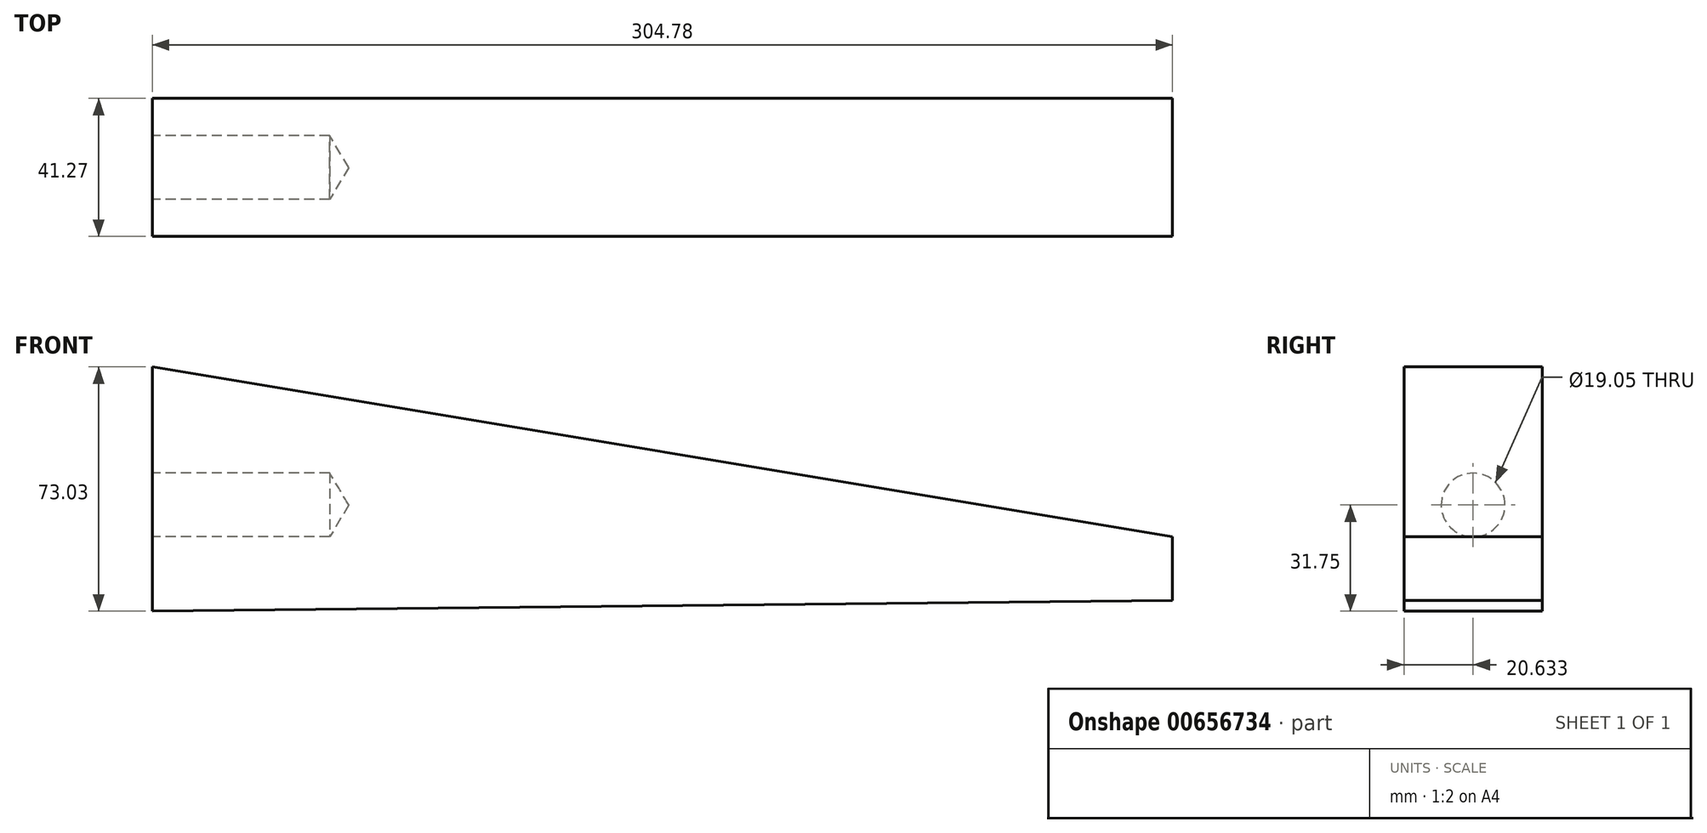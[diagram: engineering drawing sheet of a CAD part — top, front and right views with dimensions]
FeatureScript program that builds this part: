
annotation { "Feature Type Name" : "Feature", "Feature Type Description" : "" }
export const myFeature = defineFeature(function(context is Context, id is Id, definition is map)
    precondition{}
    {
        {
            var Q0;
            Q0=qCreatedBy(makeId("Front.planeOp"),FACE);
            var sketch = newSketch(context, id + "F0", { "sketchPlane" : qUnion([Q0])});
            skLineSegment(sketch, "E0.bottom", {"start": v(0, 0) * mm, "end": v(304.78, 3.17) * mm});
            skLineSegment(sketch, "E0.left", {"start": v(0, 0) * mm, "end": v(0, 73.03) * mm});
            skLineSegment(sketch, "E1", {"start": v(304.78, 3.17) * mm, "end": v(304.78, 22.22) * mm});
            skLineSegment(sketch, "E2", {"start": v(304.78, 22.22) * mm, "end": v(0, 73.03) * mm});
            skSolve(sketch);
        }
        {
            var Q0;
            Q0=makeQuery(id+"F0.imprint","IMPRINT",FACE,{"disambiguationData":[TD([[makeQuery(id+"F0.imprint","IMPRINT",EDGE,{"derivedFrom":sQuery(id+"F0.wireOp",EDGE,"E0.bottom")}),1.0]])]});
            extrude(context, id + "F1", {"entities" : qUnion([Q0]), "flatOperationType" : FlatOperationType.REMOVE, "depth" : 41.27 * mm, "offsetDistance" : 25.4 * mm, "domain" : OperationDomain.MODEL});
        }
        {
            var Q0;
            Q0=makeQuery(id+"F1.opExtrude","SWEPT_FACE",FACE,{"disambiguationData":[OSD([sQuery(id+"F0.wireOp",EDGE,"E0.left")])]});
            var sketch = newSketch(context, id + "F2", { "sketchPlane" : qUnion([Q0])});
            skLineSegment(sketch, "E3", {"start": v(20.64, 0) * mm, "end": v(20.64, 31.75) * mm});
            skPoint(sketch, "E4", {"position": v(20.64, 31.75) * mm});
            skSolve(sketch);
        }
        {
            var Q0;
            Q0=sQuery(id+"F2.wireOp",VERTEX,"E4");
            var Q1;
            Q1=makeQuery(id+"F1.opExtrude","SWEPT_BODY",BODY,{"disambiguationData":[OSD([sQuery(id+"F0.wireOp",EDGE,"E0.bottom"),sQuery(id+"F0.wireOp",EDGE,"E0.left"),sQuery(id+"F0.wireOp",EDGE,"E1"),sQuery(id+"F0.wireOp",EDGE,"E2")])]});
            hole(context, id + "F3", {"style" : HoleStyle.SIMPLE, "endStyle" : HoleEndStyle.BLIND, "holeDiameter" : 19.05 * mm, "majorDiameter" : 6.35 * mm, "holeDepth" : 53 * mm, "isTappedThrough" : true, "tappedDepth" : 12.7 * mm, "tapClearance" : 3, "locations" : qUnion([Q0]), "scope" : qUnion([Q1])});
        }
    });
